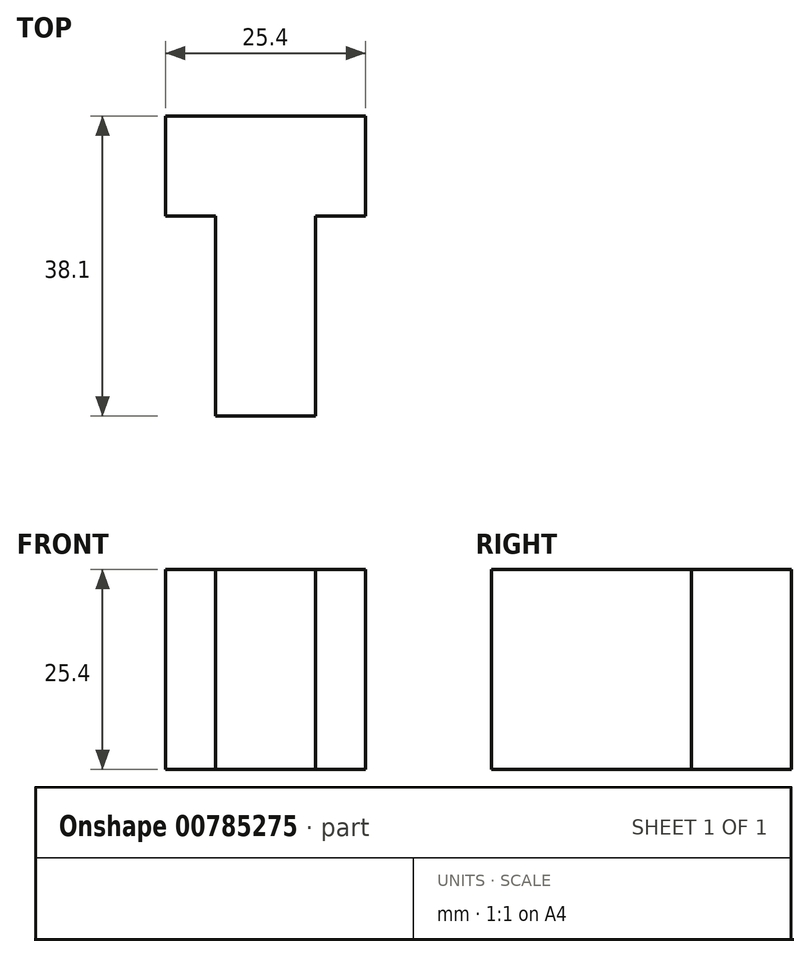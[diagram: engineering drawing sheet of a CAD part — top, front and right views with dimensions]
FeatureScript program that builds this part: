
annotation { "Feature Type Name" : "Feature", "Feature Type Description" : "" }
export const myFeature = defineFeature(function(context is Context, id is Id, definition is map)
    precondition{}
    {
        {
            var Q0;
            Q0=qCreatedBy(makeId("Top.planeOp"),FACE);
            var sketch = newSketch(context, id + "F0", { "sketchPlane" : qUnion([Q0])});
            skLineSegment(sketch, "E0", {"start": v(0, 0) * mm, "end": v(12.7, 0) * mm});
            skLineSegment(sketch, "E1", {"start": v(12.7, 0) * mm, "end": v(12.7, 25.4) * mm});
            skLineSegment(sketch, "E2", {"start": v(12.7, 25.4) * mm, "end": v(19.05, 25.4) * mm});
            skLineSegment(sketch, "E3", {"start": v(19.05, 25.4) * mm, "end": v(19.05, 38.1) * mm});
            skLineSegment(sketch, "E4", {"start": v(19.05, 38.1) * mm, "end": v(-6.35, 38.1) * mm});
            skLineSegment(sketch, "E5", {"start": v(-6.35, 38.1) * mm, "end": v(-6.35, 25.4) * mm});
            skLineSegment(sketch, "E6", {"start": v(-6.35, 25.4) * mm, "end": v(0, 25.4) * mm});
            skLineSegment(sketch, "E7", {"start": v(0, 25.4) * mm, "end": v(0, 0) * mm});
            skSolve(sketch);
        }
        {
            var Q0;
            Q0=makeQuery(id+"F0.imprint","IMPRINT",FACE,{"disambiguationData":[TD([[makeQuery(id+"F0.imprint","IMPRINT",EDGE,{"derivedFrom":sQuery(id+"F0.wireOp",EDGE,"E0")}),1.0]])]});
            extrude(context, id + "F1", {"entities" : qUnion([Q0]), "depth" : 25.4 * mm, "offsetDistance" : 25.4 * mm});
        }
    });
